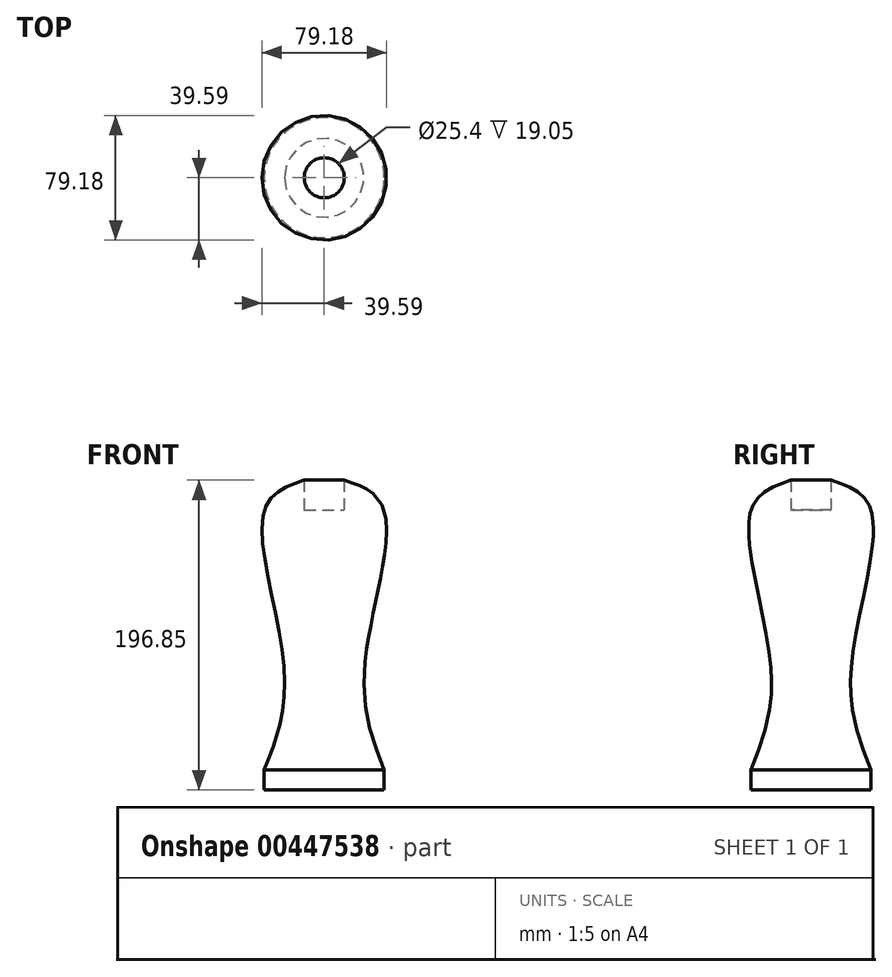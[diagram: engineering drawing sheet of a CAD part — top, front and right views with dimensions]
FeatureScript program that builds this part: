
annotation { "Feature Type Name" : "Feature", "Feature Type Description" : "" }
export const myFeature = defineFeature(function(context is Context, id is Id, definition is map)
    precondition{}
    {
        {
            var Q0;
            Q0=qCreatedBy(makeId("Front.planeOp"),FACE);
            var sketch = newSketch(context, id + "F0", { "sketchPlane" : qUnion([Q0])});
            skLineSegment(sketch, "E0", {"start": v(0, 0) * mm, "end": v(-38.1, 0) * mm});
            skLineSegment(sketch, "E1", {"start": v(-38.1, 0) * mm, "end": v(-38.1, 12.7) * mm});
            skLineSegment(sketch, "E2", {"start": v(0, 0) * mm, "end": v(0, 76.2) * mm, "construction": true});
            skLineSegment(sketch, "E3", {"start": v(0, 76.2) * mm, "end": v(0, 177.8) * mm, "construction": true});
            skLineSegment(sketch, "E4", {"start": v(0, 76.2) * mm, "end": v(-25.4, 76.2) * mm, "construction": true});
            skLineSegment(sketch, "E5", {"start": v(0, 177.8) * mm, "end": v(-38.1, 177.8) * mm, "construction": true});
            skLineSegment(sketch, "E6", {"start": v(0, 177.8) * mm, "end": v(0, 196.85) * mm, "construction": true});
            skLineSegment(sketch, "E7", {"start": v(0, 196.85) * mm, "end": v(-12.7, 196.85) * mm, "construction": true});
            skFitSpline(sketch, "E8", {"points": [v(-38.1, 12.7) * mm, v(-25.4, 76.2) * mm, v(-38.1, 177.8) * mm, v(-12.7, 196.85) * mm], "startDerivative": vector(64.68, 162.98) * mm, "endDerivative": vector(137.92, 46.53) * mm});
            skLineSegment(sketch, "E9", {"start": v(-12.7, 196.85) * mm, "end": v(-12.7, 177.8) * mm});
            skLineSegment(sketch, "E10", {"start": v(-12.7, 177.8) * mm, "end": v(0, 177.8) * mm});
            skLineSegment(sketch, "E11", {"start": v(0, 177.8) * mm, "end": v(0, 0) * mm});
            skSolve(sketch);
        }
        {
            var Q0;
            Q0=makeQuery(id+"F0.imprint","IMPRINT",FACE,{"disambiguationData":[TD([[makeQuery(id+"F0.imprint","IMPRINT",EDGE,{"derivedFrom":sQuery(id+"F0.wireOp",EDGE,"E0")}),-1.0]])]});
            var Q1;
            Q1=sQuery(id+"F0.wireOp",EDGE,"E6");
            revolve(context, id + "F1", {"entities" : qUnion([Q0]), "axis" : qUnion([Q1]), "revolveType" : RevolveType.FULL});
        }
    });
